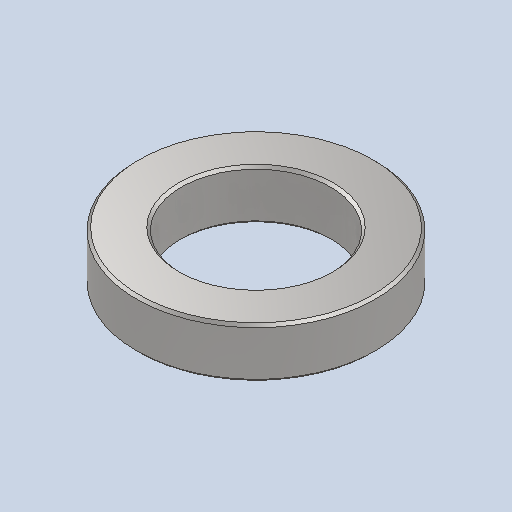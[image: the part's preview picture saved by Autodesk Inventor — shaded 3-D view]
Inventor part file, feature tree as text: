
AUTODESK INVENTOR PART (.ipt)
format: ipt  version: 2024 (Build 280153000, 153)  size: 109,056 bytes
history: native  units: in
note: dims shown in document units (in); Inventor stores cm internally (conversion verified against a paired STEP export)
features: chamfer x1
ambient origin geometry x8: Origin, YZ Plane, XZ Plane, XY Plane, X Axis, Y Axis, Z Axis, Center Point
bodies: Solid1 (feature_tree)
feature tree (1):
  chamfer  "Chamfer1"  [1 undecoded]
note: 1 required parameter value undecoded (feature->parameter linkage not recoverable at this tier; creation-order binding heuristic only, values carry confidence <= 0.55)
